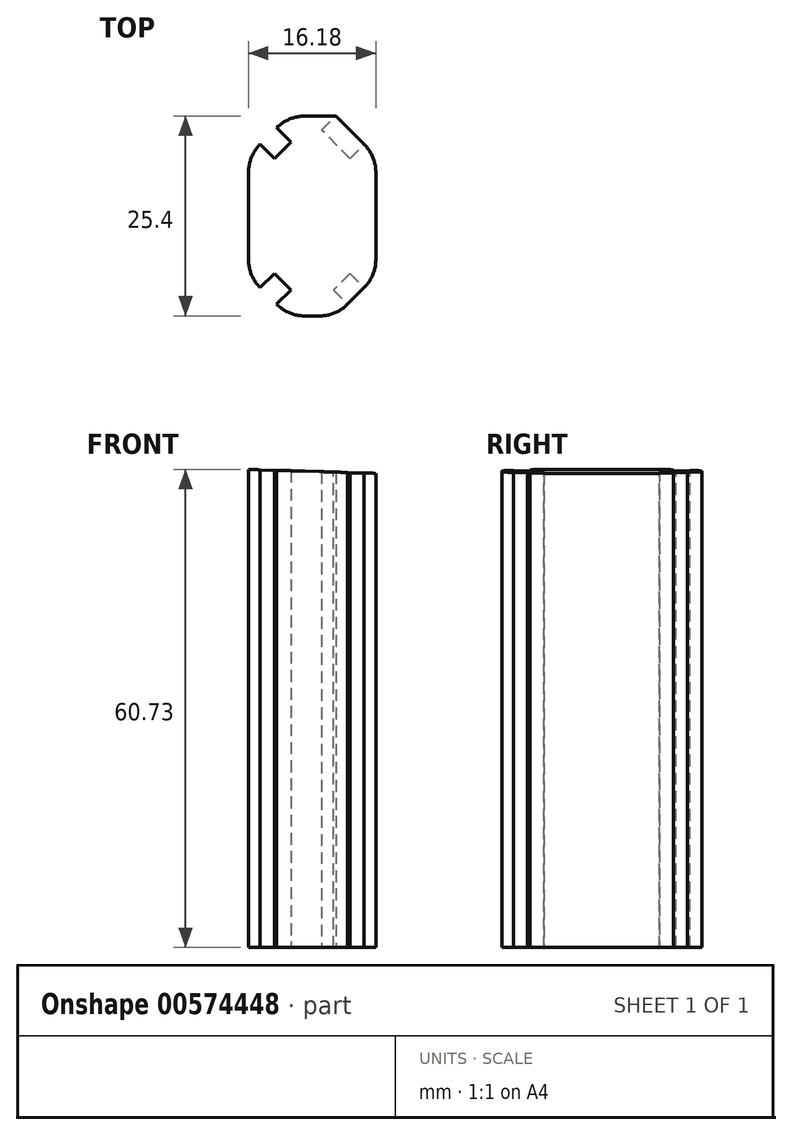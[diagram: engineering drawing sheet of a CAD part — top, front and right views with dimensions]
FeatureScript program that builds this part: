
annotation { "Feature Type Name" : "Feature", "Feature Type Description" : "" }
export const myFeature = defineFeature(function(context is Context, id is Id, definition is map)
    precondition{}
    {
        {
            var Q0;
            Q0=qCreatedBy(makeId("Front.planeOp"),FACE);
            var sketch = newSketch(context, id + "F0", { "sketchPlane" : qUnion([Q0])});
            skLineSegment(sketch, "E0.bottom", {"start": v(8.1, -71.49) * mm, "end": v(-8.1, -71.49) * mm});
            skLineSegment(sketch, "E0.top", {"start": v(8.1, 71.49) * mm, "end": v(-8.1, 71.49) * mm});
            skLineSegment(sketch, "E0.left", {"start": v(8.1, -71.49) * mm, "end": v(8.1, 71.49) * mm});
            skLineSegment(sketch, "E0.right", {"start": v(-8.1, -71.49) * mm, "end": v(-8.1, 71.49) * mm});
            skPoint(sketch, "E0.middle", {"position": v(0, 0) * mm});
            skLineSegment(sketch, "E1", {"start": v(8.1, 71.49) * mm, "end": v(8.1, 93.47) * mm});
            skLineSegment(sketch, "E2", {"start": v(8.1, 93.47) * mm, "end": v(-8.1, 71.49) * mm});
            skLineSegment(sketch, "E3", {"start": v(-17.47, 45.64) * mm, "end": v(-8.1, 71.49) * mm});
            skLineSegment(sketch, "E4", {"start": v(-17.47, 45.64) * mm, "end": v(-17.47, 0) * mm});
            skLineSegment(sketch, "E5", {"start": v(-17.47, 0) * mm, "end": v(-17.47, 0) * mm});
            skLineSegment(sketch, "E6", {"start": v(-17.47, 0) * mm, "end": v(-26.87, 0) * mm});
            skLineSegment(sketch, "E7", {"start": v(-26.87, 0) * mm, "end": v(-26.87, -10.2) * mm});
            skLineSegment(sketch, "E8", {"start": v(-26.87, -10.2) * mm, "end": v(23.98, -11.73) * mm});
            skLineSegment(sketch, "E9", {"start": v(23.98, -11.73) * mm, "end": v(24.55, 0) * mm});
            skLineSegment(sketch, "E10", {"start": v(24.55, 0) * mm, "end": v(8.1, 0) * mm});
            skSolve(sketch);
        }
        {
            var Q0;
            {var subQ0=sQuery(id+"F0.wireOp",EDGE,"E0.bottom");Q0=makeQuery(id+"F0.imprint","IMPRINT",FACE,{"disambiguationData":[TD([[makeQuery(id+"F0.imprint","IMPRINT",EDGE,{"derivedFrom":subQ0}),-1.0]])]});}
            extrude(context, id + "F1", {"entities" : qUnion([Q0]), "depth" : 25.4 * mm, "offsetDistance" : 25.4 * mm});
        }
        {
            var Q0;
            Q0=makeQuery(id+"F1.opExtrude","CAP_EDGE",EDGE,{"disambiguationData":[OSD([sQuery(id+"F0.wireOp",EDGE,"E0.left")])],"isStart":false});
            var Q1;
            Q1=makeQuery(id+"F1.opExtrude","CAP_EDGE",EDGE,{"disambiguationData":[OSD([sQuery(id+"F0.wireOp",EDGE,"E0.right")])],"isStart":false});
            var Q2;
            Q2=makeQuery(id+"F1.opExtrude","CAP_EDGE",EDGE,{"disambiguationData":[OSD([sQuery(id+"F0.wireOp",EDGE,"E0.right")])],"isStart":true});
            var Q3;
            Q3=makeQuery(id+"F1.opExtrude","CAP_EDGE",EDGE,{"disambiguationData":[OSD([sQuery(id+"F0.wireOp",EDGE,"E0.left")])],"isStart":true});
            chamfer(context, id + "F2", {"entities" : qUnion([Q0, Q1, Q2, Q3]), "width" : 5.08 * mm, "tangentPropagation" : true});
        }
        {
            var Q0;
            {var subQ0=sQuery(id+"F0.wireOp",EDGE,"E0.right");Q0=makeQuery(id+"F2.opChamfer","BLEND_EDGE",EDGE,{"blendedFrom":[makeQuery(id+"F1.opExtrude","CAP_EDGE",EDGE,{"disambiguationData":[OSD([subQ0])],"isStart":true}),makeQuery(id+"F1.opExtrude","CAP_FACE",FACE,{"disambiguationData":[OSD([sQuery(id+"F0.wireOp",EDGE,"E0.bottom"),sQuery(id+"F0.wireOp",EDGE,"E0.left"),subQ0,sQuery(id+"F0.wireOp",EDGE,"E8")])],"isStart":true})],"blendedInto":[makeQuery(id+"F1.opExtrude","CAP_FACE",FACE,{"disambiguationData":[OSD([sQuery(id+"F0.wireOp",EDGE,"E0.bottom"),sQuery(id+"F0.wireOp",EDGE,"E0.left"),subQ0,sQuery(id+"F0.wireOp",EDGE,"E8")])],"isStart":true})]});}
            var Q1;
            {var subQ0=sQuery(id+"F0.wireOp",EDGE,"E0.right");Q1=makeQuery(id+"F2.opChamfer","BLEND_EDGE",EDGE,{"blendedFrom":[makeQuery(id+"F1.opExtrude","CAP_EDGE",EDGE,{"disambiguationData":[OSD([subQ0])],"isStart":false}),makeQuery(id+"F1.opExtrude","SWEPT_FACE",FACE,{"disambiguationData":[OSD([subQ0])]})],"blendedInto":[makeQuery(id+"F1.opExtrude","SWEPT_FACE",FACE,{"disambiguationData":[OSD([subQ0])]})]});}
            var Q2;
            {var subQ0=sQuery(id+"F0.wireOp",EDGE,"E0.right");Q2=makeQuery(id+"F2.opChamfer","BLEND_EDGE",EDGE,{"blendedFrom":[makeQuery(id+"F1.opExtrude","CAP_EDGE",EDGE,{"disambiguationData":[OSD([subQ0])],"isStart":true}),makeQuery(id+"F1.opExtrude","SWEPT_FACE",FACE,{"disambiguationData":[OSD([subQ0])]})],"blendedInto":[makeQuery(id+"F1.opExtrude","SWEPT_FACE",FACE,{"disambiguationData":[OSD([subQ0])]})]});}
            var Q3;
            {var subQ0=sQuery(id+"F0.wireOp",EDGE,"E0.left");Q3=makeQuery(id+"F2.opChamfer","BLEND_EDGE",EDGE,{"blendedFrom":[makeQuery(id+"F1.opExtrude","CAP_EDGE",EDGE,{"disambiguationData":[OSD([subQ0])],"isStart":true}),makeQuery(id+"F1.opExtrude","SWEPT_FACE",FACE,{"disambiguationData":[OSD([subQ0])]})],"blendedInto":[makeQuery(id+"F1.opExtrude","SWEPT_FACE",FACE,{"disambiguationData":[OSD([subQ0])]})]});}
            var Q4;
            {var subQ0=sQuery(id+"F0.wireOp",EDGE,"E0.left");Q4=makeQuery(id+"F2.opChamfer","BLEND_EDGE",EDGE,{"blendedFrom":[makeQuery(id+"F1.opExtrude","CAP_EDGE",EDGE,{"disambiguationData":[OSD([subQ0])],"isStart":false}),makeQuery(id+"F1.opExtrude","SWEPT_FACE",FACE,{"disambiguationData":[OSD([subQ0])]})],"blendedInto":[makeQuery(id+"F1.opExtrude","SWEPT_FACE",FACE,{"disambiguationData":[OSD([subQ0])]})]});}
            var Q5;
            {var subQ0=sQuery(id+"F0.wireOp",EDGE,"E0.right");Q5=makeQuery(id+"F2.opChamfer","BLEND_EDGE",EDGE,{"blendedFrom":[makeQuery(id+"F1.opExtrude","CAP_EDGE",EDGE,{"disambiguationData":[OSD([subQ0])],"isStart":false}),makeQuery(id+"F1.opExtrude","CAP_FACE",FACE,{"disambiguationData":[OSD([sQuery(id+"F0.wireOp",EDGE,"E0.bottom"),sQuery(id+"F0.wireOp",EDGE,"E0.left"),subQ0,sQuery(id+"F0.wireOp",EDGE,"E8")])],"isStart":false})],"blendedInto":[makeQuery(id+"F1.opExtrude","CAP_FACE",FACE,{"disambiguationData":[OSD([sQuery(id+"F0.wireOp",EDGE,"E0.bottom"),sQuery(id+"F0.wireOp",EDGE,"E0.left"),subQ0,sQuery(id+"F0.wireOp",EDGE,"E8")])],"isStart":false})]});}
            var Q6;
            {var subQ0=sQuery(id+"F0.wireOp",EDGE,"E0.left");Q6=makeQuery(id+"F2.opChamfer","BLEND_EDGE",EDGE,{"blendedFrom":[makeQuery(id+"F1.opExtrude","CAP_EDGE",EDGE,{"disambiguationData":[OSD([subQ0])],"isStart":false}),makeQuery(id+"F1.opExtrude","CAP_FACE",FACE,{"disambiguationData":[OSD([sQuery(id+"F0.wireOp",EDGE,"E0.bottom"),subQ0,sQuery(id+"F0.wireOp",EDGE,"E0.right"),sQuery(id+"F0.wireOp",EDGE,"E8")])],"isStart":false})],"blendedInto":[makeQuery(id+"F1.opExtrude","CAP_FACE",FACE,{"disambiguationData":[OSD([sQuery(id+"F0.wireOp",EDGE,"E0.bottom"),subQ0,sQuery(id+"F0.wireOp",EDGE,"E0.right"),sQuery(id+"F0.wireOp",EDGE,"E8")])],"isStart":false})]});}
            fillet(context, id + "F3", {"entities" : qUnion([Q0, Q1, Q2, Q3, Q4, Q5, Q6]), "radius" : 5.08 * mm, "tangentPropagation" : true, "allowEdgeOverflow" : false});
        }
        {
            var Q0;
            {var subQ0=sQuery(id+"F0.wireOp",EDGE,"E0.right");Q0=makeQuery(id+"F2.opChamfer","BLEND_FACE",FACE,{"disambiguationData":[OSD([subQ0]),TDD([makeQuery(id+"F1.opExtrude","CAP_EDGE",EDGE,{"disambiguationData":[OSD([subQ0])],"isStart":false})])]});}
            extrude(context, id + "F4", {"entities" : qUnion([Q0]), "operationType" : NewBodyOperationType.REMOVE, "oppositeDirection" : true, "depth" : 2.54 * mm, "offsetDistance" : 25.4 * mm});
        }
        {
            var Q0;
            {var subQ0=sQuery(id+"F0.wireOp",EDGE,"E0.right");Q0=makeQuery(id+"F2.opChamfer","BLEND_FACE",FACE,{"disambiguationData":[OSD([subQ0]),TDD([makeQuery(id+"F1.opExtrude","CAP_EDGE",EDGE,{"disambiguationData":[OSD([subQ0])],"isStart":true})])]});}
            extrude(context, id + "F5", {"entities" : qUnion([Q0]), "operationType" : NewBodyOperationType.REMOVE, "oppositeDirection" : true, "depth" : 2.54 * mm, "offsetDistance" : 25.4 * mm});
        }
        {
            var Q0;
            {var subQ0=sQuery(id+"F0.wireOp",EDGE,"E0.left");Q0=makeQuery(id+"F2.opChamfer","BLEND_FACE",FACE,{"disambiguationData":[OSD([subQ0]),TDD([makeQuery(id+"F1.opExtrude","CAP_EDGE",EDGE,{"disambiguationData":[OSD([subQ0])],"isStart":true})])]});}
            extrude(context, id + "F6", {"entities" : qUnion([Q0]), "operationType" : NewBodyOperationType.REMOVE, "oppositeDirection" : true, "depth" : 2.54 * mm, "offsetDistance" : 25.4 * mm});
        }
        {
            var Q0;
            {var subQ0=sQuery(id+"F0.wireOp",EDGE,"E0.left");Q0=makeQuery(id+"F2.opChamfer","BLEND_FACE",FACE,{"disambiguationData":[OSD([subQ0]),TDD([makeQuery(id+"F1.opExtrude","CAP_EDGE",EDGE,{"disambiguationData":[OSD([subQ0])],"isStart":false})])]});}
            extrude(context, id + "F7", {"entities" : qUnion([Q0]), "operationType" : NewBodyOperationType.REMOVE, "oppositeDirection" : true, "depth" : 2.54 * mm, "offsetDistance" : 25.4 * mm});
        }
    });
